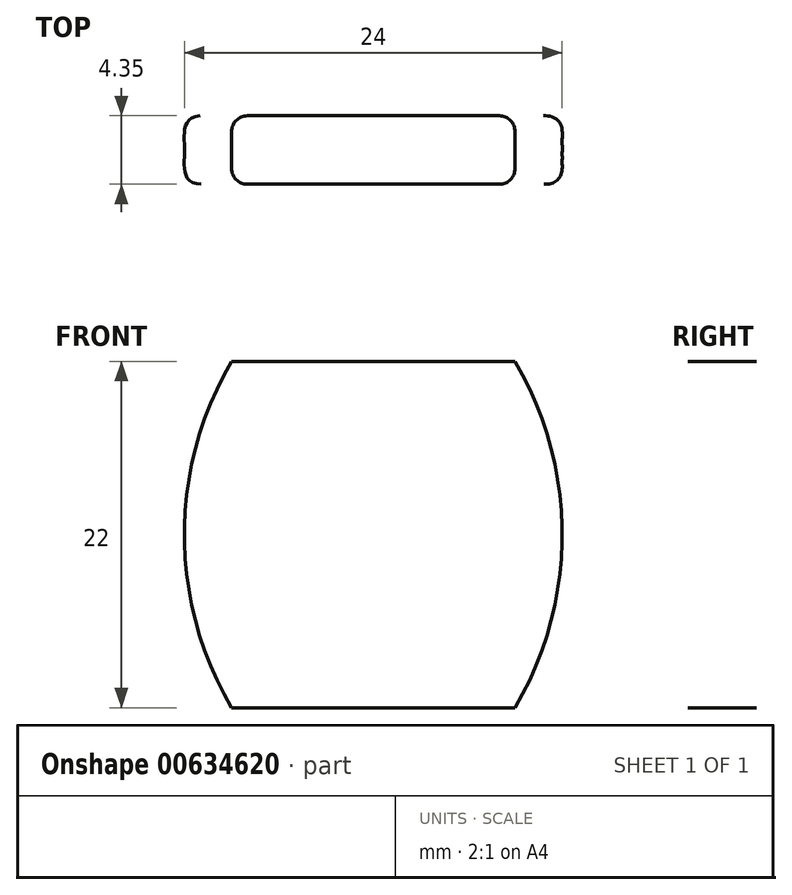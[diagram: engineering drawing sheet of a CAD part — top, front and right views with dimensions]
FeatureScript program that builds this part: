
annotation { "Feature Type Name" : "Feature", "Feature Type Description" : "" }
export const myFeature = defineFeature(function(context is Context, id is Id, definition is map)
    precondition{}
    {
        {
            var Q0;
            Q0=qCreatedBy(makeId("Top.planeOp"),FACE);
            cPlane(context, id + "F0", {"entities" : qUnion([Q0]), "cplaneType" : CPlaneType.OFFSET, "offset" : 11 * mm, "width" : 150 * mm, "height" : 150 * mm});
        }
        {
            var Q0;
            Q0=qCreatedBy(makeId("Top.planeOp"),FACE);
            cPlane(context, id + "F1", {"entities" : qUnion([Q0]), "cplaneType" : CPlaneType.OFFSET, "offset" : 11 * mm, "oppositeDirection" : true, "width" : 150 * mm, "height" : 150 * mm});
        }
        {
            var Q0;
            Q0=qCreatedBy(makeId("Top.planeOp"),FACE);
            var sketch = newSketch(context, id + "F2", { "sketchPlane" : qUnion([Q0])});
            skLineSegment(sketch, "E0", {"start": v(-11, 2.5) * mm, "end": v(11, 2.5) * mm});
            skLineSegment(sketch, "E1", {"start": v(-11, -1.85) * mm, "end": v(11, -1.85) * mm});
            skLineSegment(sketch, "E2", {"start": v(-12, -0.85) * mm, "end": v(-12, 1.5) * mm});
            skLineSegment(sketch, "E3", {"start": v(12, -0.85) * mm, "end": v(12, 1.5) * mm});
            skPoint(sketch, "E4.visualSharp", {"position": v(-12, 2.5) * mm});
            skArc(sketch, "E4.filletArc", {"start": v(-11, 2.5) * mm, "mid": v(-11.7, 2.2) * mm, "end": v(-12, 1.5) * mm});
            skPoint(sketch, "E5.visualSharp", {"position": v(-12, -1.85) * mm});
            skArc(sketch, "E5.filletArc", {"start": v(-12, -0.85) * mm, "mid": v(-11.7, -1.56) * mm, "end": v(-11, -1.85) * mm});
            skPoint(sketch, "E6.visualSharp", {"position": v(12, 2.5) * mm});
            skArc(sketch, "E6.filletArc", {"start": v(12, 1.5) * mm, "mid": v(11.7, 2.2) * mm, "end": v(11, 2.5) * mm});
            skPoint(sketch, "E7.visualSharp", {"position": v(12, -1.85) * mm});
            skArc(sketch, "E7.filletArc", {"start": v(11, -1.85) * mm, "mid": v(11.7, -1.56) * mm, "end": v(12, -0.85) * mm});
            skSolve(sketch);
        }
        {
            var Q0;
            Q0=qCreatedBy(id+"F0.planeOp",FACE);
            var sketch = newSketch(context, id + "F3", { "sketchPlane" : qUnion([Q0])});
            skLineSegment(sketch, "E8.bottom", {"start": v(-8, -1.85) * mm, "end": v(8, -1.85) * mm});
            skLineSegment(sketch, "E8.top", {"start": v(-8, 2.5) * mm, "end": v(8, 2.5) * mm});
            skLineSegment(sketch, "E8.left", {"start": v(-9, -0.85) * mm, "end": v(-9, 1.5) * mm});
            skLineSegment(sketch, "E8.right", {"start": v(9, -0.85) * mm, "end": v(9, 1.5) * mm});
            skPoint(sketch, "E9.visualSharp", {"position": v(-9, 2.5) * mm});
            skArc(sketch, "E9.filletArc", {"start": v(-8, 2.5) * mm, "mid": v(-8.7, 2.2) * mm, "end": v(-9, 1.5) * mm});
            skPoint(sketch, "E10.visualSharp", {"position": v(-9, -1.85) * mm});
            skArc(sketch, "E10.filletArc", {"start": v(-9, -0.85) * mm, "mid": v(-8.7, -1.56) * mm, "end": v(-8, -1.85) * mm});
            skPoint(sketch, "E11.visualSharp", {"position": v(9, 2.5) * mm});
            skArc(sketch, "E11.filletArc", {"start": v(9, 1.5) * mm, "mid": v(8.7, 2.2) * mm, "end": v(8, 2.5) * mm});
            skPoint(sketch, "E12.visualSharp", {"position": v(9, -1.85) * mm});
            skArc(sketch, "E12.filletArc", {"start": v(8, -1.85) * mm, "mid": v(8.7, -1.56) * mm, "end": v(9, -0.85) * mm});
            skSolve(sketch);
        }
        {
            var Q0;
            Q0=qCreatedBy(id+"F1.planeOp",FACE);
            var sketch = newSketch(context, id + "F4", { "sketchPlane" : qUnion([Q0])});
            skPoint(sketch, "E13.middle", {"position": v(0, 0) * mm});
            skLineSegment(sketch, "E14.bottom", {"start": v(-8, 2.5) * mm, "end": v(8, 2.5) * mm});
            skLineSegment(sketch, "E14.top", {"start": v(-8, -1.85) * mm, "end": v(8, -1.85) * mm});
            skLineSegment(sketch, "E14.left", {"start": v(-9, 1.5) * mm, "end": v(-9, -0.85) * mm});
            skLineSegment(sketch, "E14.right", {"start": v(9, 1.5) * mm, "end": v(9, -0.85) * mm});
            skPoint(sketch, "E15.visualSharp", {"position": v(-9, -1.85) * mm});
            skArc(sketch, "E15.filletArc", {"start": v(-9, -0.85) * mm, "mid": v(-8.7, -1.56) * mm, "end": v(-8, -1.85) * mm});
            skPoint(sketch, "E16.visualSharp", {"position": v(-9, 2.5) * mm});
            skArc(sketch, "E16.filletArc", {"start": v(-8, 2.5) * mm, "mid": v(-8.7, 2.2) * mm, "end": v(-9, 1.5) * mm});
            skPoint(sketch, "E17.visualSharp", {"position": v(9, 2.5) * mm});
            skArc(sketch, "E17.filletArc", {"start": v(9, 1.5) * mm, "mid": v(8.7, 2.2) * mm, "end": v(8, 2.5) * mm});
            skPoint(sketch, "E18.visualSharp", {"position": v(9, -1.85) * mm});
            skArc(sketch, "E18.filletArc", {"start": v(8, -1.85) * mm, "mid": v(8.7, -1.56) * mm, "end": v(9, -0.85) * mm});
            skSolve(sketch);
        }
        {
            var Q0;
            Q0=qCreatedBy(makeId("Front.planeOp"),FACE);
            var sketch = newSketch(context, id + "F5", { "sketchPlane" : qUnion([Q0])});
            skLineSegment(sketch, "E19", {"start": v(9, 11) * mm, "end": v(-9, 11) * mm});
            skLineSegment(sketch, "E20", {"start": v(12, 0) * mm, "end": v(-12, 0) * mm});
            skLineSegment(sketch, "E21", {"start": v(9, -11) * mm, "end": v(-9, -11) * mm});
            skArc(sketch, "E22", {"start": v(9, -11) * mm, "mid": v(12, 0) * mm, "end": v(9, 11) * mm});
            skArc(sketch, "E23", {"start": v(-9, 11) * mm, "mid": v(-12, 0) * mm, "end": v(-9, -11) * mm});
            skSolve(sketch);
        }
        {
            var Q0;
            Q0=makeQuery(id+"F3.imprint","IMPRINT",FACE,{"disambiguationData":[TD([[makeQuery(id+"F3.imprint","IMPRINT",EDGE,{"derivedFrom":sQuery(id+"F3.wireOp",EDGE,"E8.bottom")}),1.0]])]});
            var Q1;
            Q1=makeQuery(id+"F2.imprint","IMPRINT",FACE,{"disambiguationData":[TD([[makeQuery(id+"F2.imprint","IMPRINT",EDGE,{"derivedFrom":sQuery(id+"F2.wireOp",EDGE,"E0")}),-1.0]])]});
            var Q2;
            Q2=makeQuery(id+"F4.imprint","IMPRINT",FACE,{"disambiguationData":[TD([[makeQuery(id+"F4.imprint","IMPRINT",EDGE,{"derivedFrom":sQuery(id+"F4.wireOp",EDGE,"E14.bottom")}),-1.0]])]});
            var Q3;
            Q3=makeQuery(id+"F3.imprint","IMPRINT",FACE,{"disambiguationData":[TD([[makeQuery(id+"F3.imprint","IMPRINT",EDGE,{"derivedFrom":sQuery(id+"F3.wireOp",EDGE,"E8.bottom")}),1.0]])]});
            var Q4;
            Q4=makeQuery(id+"F2.imprint","IMPRINT",FACE,{"disambiguationData":[TD([[makeQuery(id+"F2.imprint","IMPRINT",EDGE,{"derivedFrom":sQuery(id+"F2.wireOp",EDGE,"E0")}),-1.0]])]});
            var Q5;
            Q5=makeQuery(id+"F4.imprint","IMPRINT",FACE,{"disambiguationData":[TD([[makeQuery(id+"F4.imprint","IMPRINT",EDGE,{"derivedFrom":sQuery(id+"F4.wireOp",EDGE,"E14.bottom")}),-1.0]])]});
            var Q6;
            Q6=sQuery(id+"F5.wireOp",EDGE,"E22");
            var Q7;
            Q7=sQuery(id+"F5.wireOp",EDGE,"E23");
            loft(context, id + "F6", {"addGuides" : true, "sheetProfilesArray" : [{ "sheetProfileEntities" : qUnion([Q0]) }, { "sheetProfileEntities" : qUnion([Q1]) }, { "sheetProfileEntities" : qUnion([Q2]) }], "wireProfilesArray" : [{ "wireProfileEntities" : qUnion([Q3]) }, { "wireProfileEntities" : qUnion([Q4]) }, { "wireProfileEntities" : qUnion([Q5]) }], "guidesArray" : [{ "guideEntities" : qUnion([Q6]), "guideDerivativeType" : LoftGuideDerivativeType.DEFAULT, "guideDerivativeMagnitude" : 1 }, { "guideEntities" : qUnion([Q7]), "guideDerivativeType" : LoftGuideDerivativeType.DEFAULT, "guideDerivativeMagnitude" : 1 }]});
        }
    });
